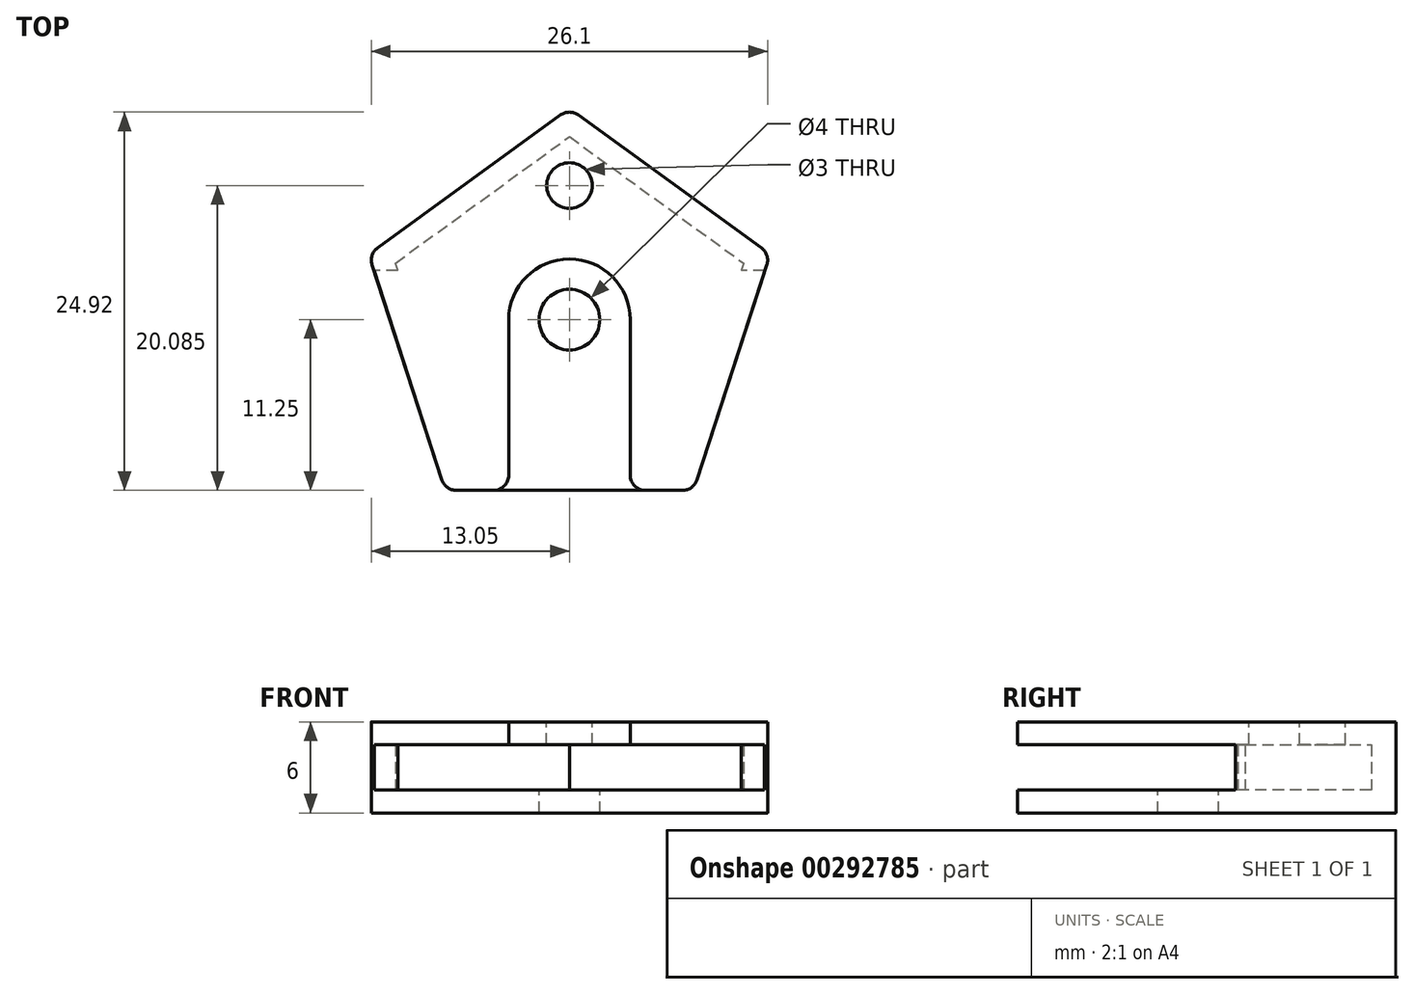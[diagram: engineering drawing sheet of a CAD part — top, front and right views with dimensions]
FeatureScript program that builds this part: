
annotation { "Feature Type Name" : "Feature", "Feature Type Description" : "" }
export const myFeature = defineFeature(function(context is Context, id is Id, definition is map)
    precondition{}
    {
        {
            var Q0;
            Q0=qCreatedBy(makeId("Top.planeOp"),FACE);
            var sketch = newSketch(context, id + "F0", { "sketchPlane" : qUnion([Q0])});
            skCircle(sketch, "E0.cCircle", {"center": v(0, 0) * mm, "radius": 11.25 * mm, "construction": true});
            skLineSegment(sketch, "E0.0", {"start": v(13.23, 4.3) * mm, "end": v(8.17, -11.25) * mm});
            skLineSegment(sketch, "E0.1", {"start": v(8.17, -11.25) * mm, "end": v(-8.17, -11.25) * mm});
            skLineSegment(sketch, "E0.2", {"start": v(-8.17, -11.25) * mm, "end": v(-13.23, 4.3) * mm});
            skLineSegment(sketch, "E0.3", {"start": v(-13.23, 4.3) * mm, "end": v(0, 13.9) * mm});
            skLineSegment(sketch, "E0.4", {"start": v(0, 13.9) * mm, "end": v(13.23, 4.3) * mm});
            skPoint(sketch, "E0.0.midPoint", {"position": v(10.7, -3.48) * mm});
            skSolve(sketch);
        }
        {
            var Q0;
            Q0 = qSketchRegion(id + "F0", true);
            extrude(context, id + "F1", {"entities" : qUnion([Q0]), "depth" : 6 * mm});
        }
        {
            var Q0;
            Q0=makeQuery(id+"F1.opExtrude","SWEPT_FACE",FACE,{"disambiguationData":[OSD([sQuery(id+"F0.wireOp",EDGE,"E0.0")])]});
            shell(context, id + "F2", {"entities" : qUnion([Q0]), "thickness" : 1.5 * mm});
        }
        {
            var Q0;
            Q0 = qSketchRegion(id + "F0", true);
            extrude(context, id + "F3", {"entities" : qUnion([Q0]), "operationType" : NewBodyOperationType.ADD, "depth" : 5 * mm});
        }
        {
            var Q0;
            Q0=makeQuery(id+"F1.opExtrude","SWEPT_FACE",FACE,{"disambiguationData":[OSD([sQuery(id+"F0.wireOp",EDGE,"E0.1")])]});
            shell(context, id + "F4", {"entities" : qUnion([Q0]), "thickness" : 1.5 * mm});
        }
        {
            var Q0;
            Q0=makeQuery(id+"F1.opExtrude","SWEPT_FACE",FACE,{"disambiguationData":[OSD([sQuery(id+"F0.wireOp",EDGE,"E0.1")])]});
            var sketch = newSketch(context, id + "F5", { "sketchPlane" : qUnion([Q0])});
            skLineSegment(sketch, "E1.bottom", {"start": v(-12.87, 4.5) * mm, "end": v(12.84, 4.5) * mm});
            skLineSegment(sketch, "E1.top", {"start": v(-12.87, 1.5) * mm, "end": v(12.84, 1.5) * mm});
            skLineSegment(sketch, "E1.left", {"start": v(-12.87, 4.5) * mm, "end": v(-12.87, 1.5) * mm});
            skLineSegment(sketch, "E1.right", {"start": v(12.84, 4.5) * mm, "end": v(12.84, 1.5) * mm});
            skSolve(sketch);
        }
        {
            var Q0;
            Q0 = qSketchRegion(id + "F5", true);
            extrude(context, id + "F6", {"entities" : qUnion([Q0]), "operationType" : NewBodyOperationType.REMOVE, "oppositeDirection" : true, "depth" : 14.5 * mm});
        }
        {
            var Q0;
            Q0=makeQuery(id+"F1.opExtrude","CAP_FACE",FACE,{"disambiguationData":[OSD([sQuery(id+"F0.wireOp",EDGE,"E0.0"),sQuery(id+"F0.wireOp",EDGE,"E0.1"),sQuery(id+"F0.wireOp",EDGE,"E0.2"),sQuery(id+"F0.wireOp",EDGE,"E0.3"),sQuery(id+"F0.wireOp",EDGE,"E0.4")])],"isStart":false});
            var sketch = newSketch(context, id + "F7", { "sketchPlane" : qUnion([Q0])});
            skArc(sketch, "E2", {"start": v(4, 0) * mm, "mid": v(0, 4) * mm, "end": v(-4, 0) * mm});
            skLineSegment(sketch, "E3", {"start": v(-4, 0) * mm, "end": v(-4, -12.56) * mm});
            skLineSegment(sketch, "E4", {"start": v(-4, -12.56) * mm, "end": v(4, -12.56) * mm});
            skLineSegment(sketch, "E5", {"start": v(4, 0) * mm, "end": v(4, -12.56) * mm});
            skSolve(sketch);
        }
        {
            var Q0;
            Q0 = qSketchRegion(id + "F7", true);
            extrude(context, id + "F8", {"entities" : qUnion([Q0]), "operationType" : NewBodyOperationType.REMOVE, "oppositeDirection" : true, "depth" : 2 * mm});
        }
        {
            var Q0;
            {var subQ0=sQuery(id+"F0.wireOp",EDGE,"E0.4");var subQ1=sQuery(id+"F0.wireOp",EDGE,"E0.3");var subQ2=sQuery(id+"F0.wireOp",EDGE,"E0.2");var subQ3=sQuery(id+"F0.wireOp",EDGE,"E0.1");var subQ4=sQuery(id+"F0.wireOp",EDGE,"E0.0");Q0=makeQuery(id+"F6.boolean.opBoolean","MERGE",FACE,{"derivedFrom":[makeQuery(id+"F4.opShell","OFFSET_FACE",FACE,{"disambiguationData":[OSD([subQ4,subQ3,subQ2,subQ1,subQ0]),TDD([makeQuery(id+"F1.opExtrude","CAP_FACE",FACE,{"disambiguationData":[OSD([subQ4,subQ3,subQ2,subQ1,subQ0])],"isStart":true})])]}),makeQuery(id+"F6.opExtrude","SWEPT_FACE",FACE,{"disambiguationData":[OSD([sQuery(id+"F5.wireOp",EDGE,"E1.top")])]})]});}
            var sketch = newSketch(context, id + "F9", { "sketchPlane" : qUnion([Q0])});
            skCircle(sketch, "E6", {"center": v(0, 0) * mm, "radius": 2 * mm});
            skSolve(sketch);
        }
        {
            var Q0;
            Q0 = qSketchRegion(id + "F9", true);
            extrude(context, id + "F10", {"entities" : qUnion([Q0]), "operationType" : NewBodyOperationType.REMOVE, "oppositeDirection" : true, "depth" : 25 * mm});
        }
        {
            var Q0;
            {var subQ0=sQuery(id+"F0.wireOp",EDGE,"E0.1");var subQ1=sQuery(id+"F0.wireOp",EDGE,"E0.0");Q0=makeQuery(id+"F6.boolean.opBoolean","SPLIT",EDGE,{"disambiguationData":[TD([makeQuery(id+"F6.opExtrude","SWEPT_FACE",FACE,{"disambiguationData":[OSD([sQuery(id+"F5.wireOp",EDGE,"E1.bottom")])]})])],"derivedFrom":makeQuery(id+"F1.opExtrude","SWEPT_EDGE",EDGE,{"disambiguationData":[OSD([subQ1,subQ0])]})});}
            var Q1;
            Q1=makeQuery(id+"F1.opExtrude","SWEPT_EDGE",EDGE,{"disambiguationData":[OSD([sQuery(id+"F0.wireOp",EDGE,"E0.0"),sQuery(id+"F0.wireOp",EDGE,"E0.4")])]});
            var Q2;
            {var subQ0=sQuery(id+"F0.wireOp",EDGE,"E0.0");var subQ1=sQuery(id+"F0.wireOp",EDGE,"E0.1");Q2=makeQuery(id+"F6.boolean.opBoolean","SPLIT",EDGE,{"disambiguationData":[TD([makeQuery(id+"F6.opExtrude","SWEPT_FACE",FACE,{"disambiguationData":[OSD([sQuery(id+"F5.wireOp",EDGE,"E1.top")])]})])],"derivedFrom":makeQuery(id+"F1.opExtrude","SWEPT_EDGE",EDGE,{"disambiguationData":[OSD([subQ0,subQ1])]})});}
            var Q3;
            {var subQ2=sQuery(id+"F0.wireOp",EDGE,"E0.2");var subQ3=sQuery(id+"F0.wireOp",EDGE,"E0.1");Q3=makeQuery(id+"F6.boolean.opBoolean","SPLIT",EDGE,{"disambiguationData":[TD([makeQuery(id+"F6.opExtrude","SWEPT_FACE",FACE,{"disambiguationData":[OSD([sQuery(id+"F5.wireOp",EDGE,"E1.top")])]})])],"derivedFrom":makeQuery(id+"F1.opExtrude","SWEPT_EDGE",EDGE,{"disambiguationData":[OSD([subQ3,subQ2])]})});}
            var Q4;
            {var subQ2=sQuery(id+"F0.wireOp",EDGE,"E0.2");var subQ3=sQuery(id+"F0.wireOp",EDGE,"E0.1");Q4=makeQuery(id+"F6.boolean.opBoolean","SPLIT",EDGE,{"disambiguationData":[TD([makeQuery(id+"F6.opExtrude","SWEPT_FACE",FACE,{"disambiguationData":[OSD([sQuery(id+"F5.wireOp",EDGE,"E1.bottom")])]})])],"derivedFrom":makeQuery(id+"F1.opExtrude","SWEPT_EDGE",EDGE,{"disambiguationData":[OSD([subQ3,subQ2])]})});}
            var Q5;
            {var subQ4=sQuery(id+"F0.wireOp",EDGE,"E0.1");Q5=makeQuery(id+"F8.boolean.opBoolean","INTERSECT",EDGE,{"derivedFrom":[makeQuery(id+"F6.boolean.opBoolean","SPLIT",FACE,{"disambiguationData":[TD([makeQuery(id+"F6.opExtrude","SWEPT_FACE",FACE,{"disambiguationData":[OSD([sQuery(id+"F5.wireOp",EDGE,"E1.bottom")])]})])],"derivedFrom":makeQuery(id+"F1.opExtrude","SWEPT_FACE",FACE,{"disambiguationData":[OSD([subQ4])]})}),makeQuery(id+"F8.opExtrude","SWEPT_FACE",FACE,{"disambiguationData":[OSD([sQuery(id+"F7.wireOp",EDGE,"E3")])]})]});}
            var Q6;
            {var subQ4=sQuery(id+"F0.wireOp",EDGE,"E0.1");Q6=makeQuery(id+"F8.boolean.opBoolean","INTERSECT",EDGE,{"derivedFrom":[makeQuery(id+"F6.boolean.opBoolean","SPLIT",FACE,{"disambiguationData":[TD([makeQuery(id+"F6.opExtrude","SWEPT_FACE",FACE,{"disambiguationData":[OSD([sQuery(id+"F5.wireOp",EDGE,"E1.bottom")])]})])],"derivedFrom":makeQuery(id+"F1.opExtrude","SWEPT_FACE",FACE,{"disambiguationData":[OSD([subQ4])]})}),makeQuery(id+"F8.opExtrude","SWEPT_FACE",FACE,{"disambiguationData":[OSD([sQuery(id+"F7.wireOp",EDGE,"E5")])]})]});}
            var Q7;
            Q7=makeQuery(id+"F1.opExtrude","SWEPT_EDGE",EDGE,{"disambiguationData":[OSD([sQuery(id+"F0.wireOp",EDGE,"E0.3"),sQuery(id+"F0.wireOp",EDGE,"E0.4")])]});
            var Q8;
            Q8=makeQuery(id+"F1.opExtrude","SWEPT_EDGE",EDGE,{"disambiguationData":[OSD([sQuery(id+"F0.wireOp",EDGE,"E0.2"),sQuery(id+"F0.wireOp",EDGE,"E0.3")])]});
            fillet(context, id + "F11", {"entities" : qUnion([Q0, Q1, Q2, Q3, Q4, Q5, Q6, Q7, Q8]), "radius" : 1 * mm, "tangentPropagation" : true, "allowEdgeOverflow" : false});
        }
        {
            var Q0;
            Q0=makeQuery(id+"F1.opExtrude","CAP_FACE",FACE,{"disambiguationData":[OSD([sQuery(id+"F0.wireOp",EDGE,"E0.0"),sQuery(id+"F0.wireOp",EDGE,"E0.1"),sQuery(id+"F0.wireOp",EDGE,"E0.2"),sQuery(id+"F0.wireOp",EDGE,"E0.3"),sQuery(id+"F0.wireOp",EDGE,"E0.4")])],"isStart":false});
            var sketch = newSketch(context, id + "F12", { "sketchPlane" : qUnion([Q0])});
            skLineSegment(sketch, "E7", {"start": v(0, 13.67) * mm, "end": v(0, 4) * mm, "construction": true});
            skCircle(sketch, "E8", {"center": v(0, 8.83) * mm, "radius": 1.5 * mm});
            skSolve(sketch);
        }
        {
            var Q0;
            Q0 = qSketchRegion(id + "F12", true);
            extrude(context, id + "F13", {"entities" : qUnion([Q0]), "operationType" : NewBodyOperationType.REMOVE, "oppositeDirection" : true, "depth" : 2 * mm});
        }
    });
